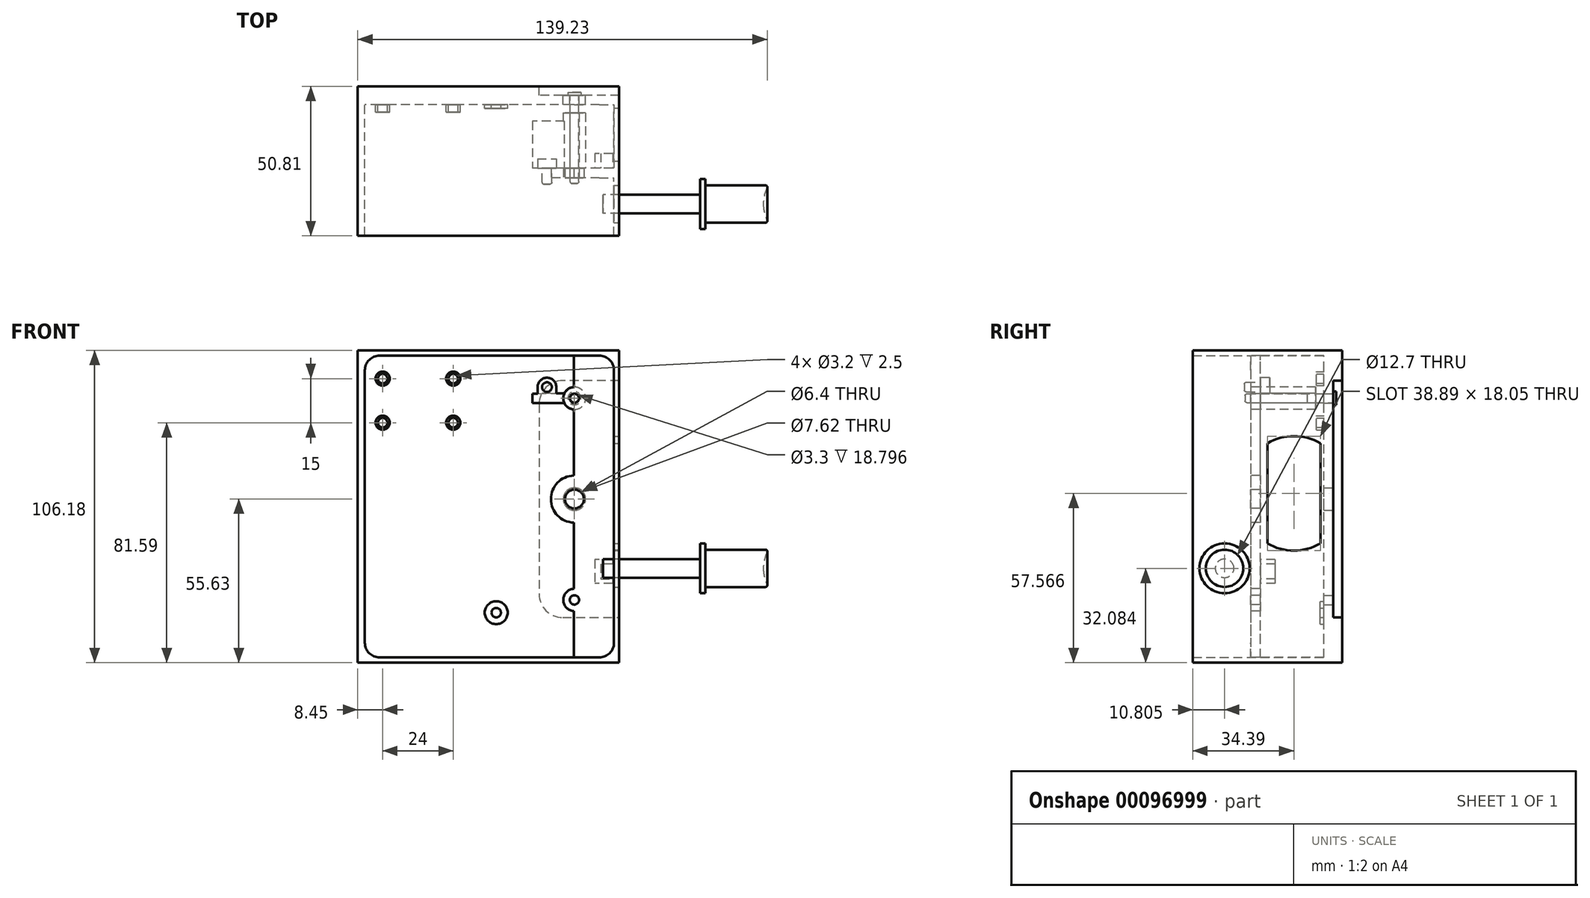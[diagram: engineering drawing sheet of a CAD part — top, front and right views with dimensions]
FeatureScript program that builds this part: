
annotation { "Feature Type Name" : "Feature", "Feature Type Description" : "" }
export const myFeature = defineFeature(function(context is Context, id is Id, definition is map)
    precondition{}
    {
        {
            var Q0;
            Q0=qCreatedBy(makeId("Front.planeOp"),FACE);
            var sketch = newSketch(context, id + "F0", { "sketchPlane" : qUnion([Q0])});
            skLineSegment(sketch, "E0", {"start": v(42.67, 51.3) * mm, "end": v(42.67, -51.3) * mm});
            skLineSegment(sketch, "E1", {"start": v(-44.45, 53.09) * mm, "end": v(-44.45, -53.09) * mm});
            skLineSegment(sketch, "E2", {"start": v(44.45, 53.09) * mm, "end": v(-44.45, 53.09) * mm});
            skLineSegment(sketch, "E3", {"start": v(44.45, -53.09) * mm, "end": v(-44.45, -53.09) * mm});
            skLineSegment(sketch, "E4", {"start": v(44.45, 53.09) * mm, "end": v(44.45, -53.09) * mm});
            skCircle(sketch, "E5", {"center": v(29.2, -31.75) * mm, "radius": 1.59 * mm});
            skCircle(sketch, "E6", {"center": v(-6.73, -45.9) * mm, "radius": 1.59 * mm});
            skLineSegment(sketch, "E7", {"start": v(36.07, 28.96) * mm, "end": v(36.07, 24.38) * mm});
            skLineSegment(sketch, "E8", {"start": v(42.21, 30.73) * mm, "end": v(36.1, 30.73) * mm});
            skLineSegment(sketch, "E9", {"start": v(42.21, 22.6) * mm, "end": v(36.1, 22.6) * mm});
            skLineSegment(sketch, "E10", {"start": v(38.13, 29.21) * mm, "end": v(38.13, 28.96) * mm});
            skLineSegment(sketch, "E11", {"start": v(36.07, 28.96) * mm, "end": v(38.15, 28.96) * mm});
            skLineSegment(sketch, "E12", {"start": v(36.07, 24.38) * mm, "end": v(38.15, 24.38) * mm});
            skLineSegment(sketch, "E13", {"start": v(42.21, 30.73) * mm, "end": v(42.21, 29.21) * mm});
            skLineSegment(sketch, "E14", {"start": v(42.21, 29.21) * mm, "end": v(38.13, 29.21) * mm});
            skLineSegment(sketch, "E15", {"start": v(42.21, 24.13) * mm, "end": v(38.13, 24.13) * mm});
            skLineSegment(sketch, "E16", {"start": v(42.21, 24.13) * mm, "end": v(42.21, 22.6) * mm});
            skLineSegment(sketch, "E17", {"start": v(36.1, 30.73) * mm, "end": v(36.1, 28.96) * mm});
            skLineSegment(sketch, "E18", {"start": v(38.15, 28.96) * mm, "end": v(38.15, 24.38) * mm});
            skLineSegment(sketch, "E19", {"start": v(38.13, 24.13) * mm, "end": v(38.13, 24.38) * mm});
            skLineSegment(sketch, "E20", {"start": v(36.1, 22.6) * mm, "end": v(36.1, 24.38) * mm});
            skLineSegment(sketch, "E21", {"start": v(36.07, -24.38) * mm, "end": v(36.07, -19.81) * mm});
            skLineSegment(sketch, "E22", {"start": v(42.21, -26.16) * mm, "end": v(36.1, -26.16) * mm});
            skLineSegment(sketch, "E23", {"start": v(42.21, -18.03) * mm, "end": v(36.1, -18.03) * mm});
            skLineSegment(sketch, "E24", {"start": v(38.13, -24.64) * mm, "end": v(38.13, -24.38) * mm});
            skLineSegment(sketch, "E25", {"start": v(36.07, -24.38) * mm, "end": v(38.15, -24.38) * mm});
            skLineSegment(sketch, "E26", {"start": v(36.07, -19.81) * mm, "end": v(38.15, -19.81) * mm});
            skLineSegment(sketch, "E27", {"start": v(42.21, -26.16) * mm, "end": v(42.21, -24.64) * mm});
            skLineSegment(sketch, "E28", {"start": v(42.21, -24.64) * mm, "end": v(38.13, -24.64) * mm});
            skLineSegment(sketch, "E29", {"start": v(42.21, -19.56) * mm, "end": v(38.13, -19.56) * mm});
            skLineSegment(sketch, "E30", {"start": v(42.21, -19.56) * mm, "end": v(42.21, -18.03) * mm});
            skLineSegment(sketch, "E31", {"start": v(36.1, -26.16) * mm, "end": v(36.1, -24.38) * mm});
            skLineSegment(sketch, "E32", {"start": v(38.15, -24.38) * mm, "end": v(38.15, -19.81) * mm});
            skLineSegment(sketch, "E33", {"start": v(38.13, -19.56) * mm, "end": v(38.13, -19.81) * mm});
            skLineSegment(sketch, "E34", {"start": v(36.1, -18.03) * mm, "end": v(36.1, -19.81) * mm});
            skLineSegment(sketch, "E35", {"start": v(42.67, 51.3) * mm, "end": v(-42.04, 51.3) * mm});
            skLineSegment(sketch, "E36", {"start": v(-42.04, 51.3) * mm, "end": v(-42.04, -51.3) * mm});
            skLineSegment(sketch, "E37", {"start": v(42.67, -51.3) * mm, "end": v(-42.04, -51.3) * mm});
            skLineSegment(sketch, "E38", {"start": v(42.67, -19.44) * mm, "end": v(44.45, -19.44) * mm});
            skLineSegment(sketch, "E39", {"start": v(42.67, -22.62) * mm, "end": v(44.45, -22.62) * mm});
            skCircle(sketch, "E40", {"center": v(29.2, 2.54) * mm, "radius": 4.76 * mm});
            skCircle(sketch, "E41", {"center": v(29.2, 2.54) * mm, "radius": 3.81 * mm});
            skLineSegment(sketch, "E42", {"start": v(29.2, 2.54) * mm, "end": v(29.2, 21.89) * mm, "construction": true});
            skCircle(sketch, "E43", {"center": v(29.2, 36.83) * mm, "radius": 1.59 * mm, "construction": true});
            skSolve(sketch);
        }
        {
            var Q0;
            Q0=qCreatedBy(makeId("Front.planeOp"),FACE);
            var sketch = newSketch(context, id + "F1", { "sketchPlane" : qUnion([Q0])});
            skLineSegment(sketch, "E44", {"start": v(-44.45, 53.09) * mm, "end": v(44.45, 53.09) * mm});
            skLineSegment(sketch, "E45", {"start": v(44.45, 53.09) * mm, "end": v(44.45, -53.09) * mm});
            skLineSegment(sketch, "E46", {"start": v(44.45, -53.09) * mm, "end": v(-44.45, -53.09) * mm});
            skLineSegment(sketch, "E47", {"start": v(-44.45, -53.09) * mm, "end": v(-44.45, 53.09) * mm});
            skSolve(sketch);
        }
        {
            var Q0;
            Q0 = qSketchRegion(id + "F1", true);
            var Q1;
            Q1=sQuery(id+"F0.wireOp",EDGE,"E2");
            var Q2;
            Q2=sQuery(id+"F0.wireOp",EDGE,"E1");
            var Q3;
            Q3=sQuery(id+"F0.wireOp",EDGE,"E4");
            var Q4;
            Q4=sQuery(id+"F0.wireOp",EDGE,"E3");
            extrude(context, id + "F2", {"entities" : qUnion([Q0]), "surfaceEntities" : qUnion([Q1, Q2, Q3, Q4]), "depth" : 19.68 * mm});
        }
        {
            var Q0;
            Q0=qCreatedBy(makeId("Front.planeOp"),FACE);
            var sketch = newSketch(context, id + "F3", { "sketchPlane" : qUnion([Q0])});
            skLineSegment(sketch, "E48.0.0", {"start": v(44.45, 53.09) * mm, "end": v(-44.45, 53.09) * mm});
            skLineSegment(sketch, "E48.0.1", {"start": v(-44.45, 53.09) * mm, "end": v(-44.45, -53.09) * mm});
            skLineSegment(sketch, "E48.0.2", {"start": v(-44.45, -53.09) * mm, "end": v(44.45, -53.09) * mm});
            skLineSegment(sketch, "E48.0.3", {"start": v(44.45, -53.09) * mm, "end": v(44.45, 53.09) * mm});
            skSolve(sketch);
        }
        {
            var Q0;
            Q0 = qSketchRegion(id + "F3", true);
            extrude(context, id + "F4", {"entities" : qUnion([Q0]), "operationType" : NewBodyOperationType.ADD, "oppositeDirection" : true, "depth" : 31.1 * mm});
        }
        {
            var Q0;
            Q0=qCreatedBy(makeId("Front.planeOp"),FACE);
            var sketch = newSketch(context, id + "F5", { "sketchPlane" : qUnion([Q0])});
            skLineSegment(sketch, "E49.0", {"start": v(-42.04, 46.3) * mm, "end": v(-42.04, -46.3) * mm});
            skLineSegment(sketch, "E50.0", {"start": v(37.67, 51.3) * mm, "end": v(-37.04, 51.3) * mm});
            skLineSegment(sketch, "E51.0", {"start": v(42.67, 46.3) * mm, "end": v(42.67, -46.3) * mm});
            skLineSegment(sketch, "E52.0", {"start": v(37.67, -51.3) * mm, "end": v(-37.04, -51.3) * mm});
            skPoint(sketch, "E53.visualSharp", {"position": v(-42.04, 51.3) * mm});
            skArc(sketch, "E53.filletArc", {"start": v(-37.04, 51.3) * mm, "mid": v(-40.58, 49.84) * mm, "end": v(-42.04, 46.3) * mm});
            skPoint(sketch, "E54.visualSharp", {"position": v(42.67, 51.3) * mm});
            skArc(sketch, "E54.filletArc", {"start": v(42.67, 46.3) * mm, "mid": v(41.2, 49.84) * mm, "end": v(37.67, 51.3) * mm});
            skPoint(sketch, "E55.visualSharp", {"position": v(-42.04, -51.3) * mm});
            skArc(sketch, "E55.filletArc", {"start": v(-42.04, -46.3) * mm, "mid": v(-40.58, -49.84) * mm, "end": v(-37.04, -51.3) * mm});
            skPoint(sketch, "E56.visualSharp", {"position": v(42.67, -51.3) * mm});
            skArc(sketch, "E56.filletArc", {"start": v(37.67, -51.3) * mm, "mid": v(41.2, -49.84) * mm, "end": v(42.67, -46.3) * mm});
            skSolve(sketch);
        }
        {
            var Q0;
            Q0 = qSketchRegion(id + "F5", true);
            extrude(context, id + "F6", {"entities" : qUnion([Q0]), "operationType" : NewBodyOperationType.REMOVE, "endBound" : BoundingType.THROUGH_ALL, "depth" : 25 * mm});
        }
        {
            var Q0;
            Q0=qCreatedBy(makeId("Front.planeOp"),FACE);
            cPlane(context, id + "F7", {"entities" : qUnion([Q0]), "cplaneType" : CPlaneType.OFFSET, "offset" : 8.88 * mm, "width" : 150 * mm, "height" : 150 * mm});
        }
        {
            var Q0;
            Q0=makeQuery(id+"F4.boolean.opBoolean","MERGE",FACE,{"derivedFrom":[makeQuery(id+"F2.opExtrude","SWEPT_FACE",FACE,{"disambiguationData":[OSD([sQuery(id+"F1.wireOp",EDGE,"E45")])]}),makeQuery(id+"F4.opExtrude","SWEPT_FACE",FACE,{"disambiguationData":[OSD([sQuery(id+"F3.wireOp",EDGE,"E48.0.3")])]})]});
            var sketch = newSketch(context, id + "F8", { "sketchPlane" : qUnion([Q0])});
            skCircle(sketch, "E57", {"center": v(-8.88, -21) * mm, "radius": 6.35 * mm});
            skSolve(sketch);
        }
        {
            var Q0;
            Q0 = qSketchRegion(id + "F8", true);
            extrude(context, id + "F9", {"entities" : qUnion([Q0]), "operationType" : NewBodyOperationType.REMOVE, "endBound" : BoundingType.UP_TO_NEXT, "oppositeDirection" : true, "depth" : 25 * mm});
        }
        {
            var Q0;
            Q0=qCreatedBy(makeId("Front.planeOp"),FACE);
            cPlane(context, id + "F10", {"entities" : qUnion([Q0]), "cplaneType" : CPlaneType.OFFSET, "offset" : 3.27 * mm, "oppositeDirection" : true, "width" : 150 * mm, "height" : 150 * mm});
        }
        {
            var Q0;
            Q0=qCreatedBy(id+"F10.planeOp",FACE);
            var sketch = newSketch(context, id + "F11", { "sketchPlane" : qUnion([Q0])});
            skArc(sketch, "E58.0.0", {"start": v(-37.04, 51.3) * mm, "mid": v(-40.58, 49.84) * mm, "end": v(-42.04, 46.3) * mm});
            skLineSegment(sketch, "E58.0.1", {"start": v(-42.04, 46.3) * mm, "end": v(-42.04, -46.3) * mm});
            skArc(sketch, "E58.0.2", {"start": v(-42.04, -46.3) * mm, "mid": v(-40.58, -49.84) * mm, "end": v(-37.04, -51.3) * mm});
            skLineSegment(sketch, "E58.0.3", {"start": v(-37.04, -51.3) * mm, "end": v(37.67, -51.3) * mm});
            skArc(sketch, "E58.0.4", {"start": v(37.67, -51.3) * mm, "mid": v(41.2, -49.84) * mm, "end": v(42.67, -46.3) * mm});
            skLineSegment(sketch, "E58.0.5", {"start": v(42.67, -46.3) * mm, "end": v(42.67, 46.3) * mm});
            skArc(sketch, "E58.0.6", {"start": v(42.67, 46.3) * mm, "mid": v(41.2, 49.84) * mm, "end": v(37.67, 51.3) * mm});
            skLineSegment(sketch, "E58.0.7", {"start": v(37.67, 51.3) * mm, "end": v(-37.04, 51.3) * mm});
            skSolve(sketch);
        }
        {
            var Q0;
            Q0 = qSketchRegion(id + "F11", true);
            extrude(context, id + "F12", {"entities" : qUnion([Q0]), "operationType" : NewBodyOperationType.REMOVE, "oppositeDirection" : true, "depth" : 21.59 * mm});
        }
        {
            var Q0;
            Q0=makeQuery(id+"F0.imprint","IMPRINT",FACE,{"disambiguationData":[TD([[makeQuery(id+"F0.imprint","IMPRINT",EDGE,{"derivedFrom":sQuery(id+"F0.wireOp",EDGE,"E5")}),1.0]])]});
            var sketch = newSketch(context, id + "F13", { "sketchPlane" : qUnion([Q0])});
            skLineSegment(sketch, "E59.0", {"start": v(29, 51.3) * mm, "end": v(-37.04, 51.3) * mm});
            skLineSegment(sketch, "E60.0", {"start": v(-42.04, 46.3) * mm, "end": v(-42.04, -46.3) * mm});
            skLineSegment(sketch, "E61.0", {"start": v(29, -51.3) * mm, "end": v(-37.04, -51.3) * mm});
            skArc(sketch, "E62.0", {"start": v(-42.04, 46.3) * mm, "mid": v(-40.58, 49.84) * mm, "end": v(-37.04, 51.3) * mm});
            skPoint(sketch, "E63.orphan", {"position": v(-42.04, 51.3) * mm});
            skPoint(sketch, "E64.orphan", {"position": v(-42.04, -51.3) * mm});
            skArc(sketch, "E65.0", {"start": v(-37.04, -51.3) * mm, "mid": v(-40.58, -49.84) * mm, "end": v(-42.04, -46.3) * mm});
            skCircle(sketch, "E66.0", {"center": v(29.2, 2.54) * mm, "radius": 3.81 * mm, "construction": true});
            skCircle(sketch, "E67.0", {"center": v(29.2, -31.75) * mm, "radius": 1.59 * mm, "construction": true});
            skLineSegment(sketch, "E68", {"start": v(29, 51.3) * mm, "end": v(29, 40.62) * mm});
            skArc(sketch, "E69", {"start": v(29, 40.62) * mm, "mid": v(25.4, 36.83) * mm, "end": v(29, 33.04) * mm});
            skArc(sketch, "E70", {"start": v(29, 10.54) * mm, "mid": v(21.2, 2.54) * mm, "end": v(29, -5.46) * mm});
            skArc(sketch, "E71", {"start": v(29, -27.96) * mm, "mid": v(25.4, -31.75) * mm, "end": v(29, -35.54) * mm});
            skPoint(sketch, "E72.orphan", {"position": v(42.67, 51.3) * mm});
            skPoint(sketch, "E73.orphan", {"position": v(42.67, -51.3) * mm});
            skLineSegment(sketch, "E74.trimOffspring", {"start": v(29, 33.04) * mm, "end": v(29, 10.54) * mm});
            skLineSegment(sketch, "E75.trimOffspring", {"start": v(29, -5.46) * mm, "end": v(29, -27.96) * mm});
            skLineSegment(sketch, "E76.trimOffspring", {"start": v(29, -35.54) * mm, "end": v(29, -51.3) * mm});
            skCircle(sketch, "E77.0", {"center": v(29.2, -31.75) * mm, "radius": 1.59 * mm});
            skCircle(sketch, "E78.0", {"center": v(29.2, 36.83) * mm, "radius": 1.59 * mm});
            skCircle(sketch, "E79", {"center": v(29.2, 2.54) * mm, "radius": 3.2 * mm});
            skSolve(sketch);
        }
        {
            var Q0;
            Q0 = qSketchRegion(id + "F13", true);
            extrude(context, id + "F14", {"entities" : qUnion([Q0]), "operationType" : NewBodyOperationType.REMOVE, "endBound" : BoundingType.UP_TO_NEXT, "oppositeDirection" : true, "depth" : 25 * mm});
        }
        {
            var Q0;
            Q0=qCreatedBy(makeId("Front.planeOp"),FACE);
            cPlane(context, id + "F15", {"entities" : qUnion([Q0]), "cplaneType" : CPlaneType.OFFSET, "offset" : 14.7 * mm, "oppositeDirection" : true, "width" : 150 * mm, "height" : 150 * mm});
        }
        {
            var Q0;
            Q0=makeQuery(id+"F4.boolean.opBoolean","MERGE",FACE,{"derivedFrom":[makeQuery(id+"F2.opExtrude","SWEPT_FACE",FACE,{"disambiguationData":[OSD([sQuery(id+"F1.wireOp",EDGE,"E45")])]}),makeQuery(id+"F4.opExtrude","SWEPT_FACE",FACE,{"disambiguationData":[OSD([sQuery(id+"F3.wireOp",EDGE,"E48.0.3")])]})]});
            var sketch = newSketch(context, id + "F16", { "sketchPlane" : qUnion([Q0])});
            skLineSegment(sketch, "E80", {"start": v(14.7, 41.38) * mm, "end": v(14.7, -48.23) * mm, "construction": true});
            skLineSegment(sketch, "E81", {"start": v(-22.52, 4.48) * mm, "end": v(53.42, 4.48) * mm, "construction": true});
            skLineSegment(sketch, "E82.left", {"start": v(23.72, -12.54) * mm, "end": v(23.72, 21.5) * mm});
            skLineSegment(sketch, "E82.right", {"start": v(5.67, -12.54) * mm, "end": v(5.67, 21.5) * mm});
            skPoint(sketch, "E82.middle", {"position": v(14.7, 4.48) * mm});
            skArc(sketch, "E83", {"start": v(23.73, 21.5) * mm, "mid": v(14.7, 23.92) * mm, "end": v(5.67, 21.5) * mm});
            skArc(sketch, "E84.trimOffspring", {"start": v(5.67, -12.54) * mm, "mid": v(14.7, -14.97) * mm, "end": v(23.72, -12.54) * mm});
            skPoint(sketch, "E85", {"position": v(14.7, 23.92) * mm});
            skPoint(sketch, "E86", {"position": v(14.7, -14.97) * mm});
            skSolve(sketch);
        }
        {
            var Q0;
            Q0 = qSketchRegion(id + "F16", true);
            extrude(context, id + "F17", {"entities" : qUnion([Q0]), "operationType" : NewBodyOperationType.REMOVE, "oppositeDirection" : true, "depth" : 2 * mm});
        }
        {
            var Q0;
            Q0=makeQuery(id+"F4.opExtrude","CAP_FACE",FACE,{"disambiguationData":[OSD([sQuery(id+"F3.wireOp",EDGE,"E48.0.0"),sQuery(id+"F3.wireOp",EDGE,"E48.0.1"),sQuery(id+"F3.wireOp",EDGE,"E48.0.2"),sQuery(id+"F3.wireOp",EDGE,"E48.0.3")])],"isStart":false});
            var sketch = newSketch(context, id + "F18", { "sketchPlane" : qUnion([Q0])});
            skLineSegment(sketch, "E87.0", {"start": v(-44.45, 42.83) * mm, "end": v(-44.45, -37.75) * mm});
            skLineSegment(sketch, "E88", {"start": v(-44.45, 42.83) * mm, "end": v(-25.21, 42.83) * mm});
            skLineSegment(sketch, "E89", {"start": v(-17.2, 34.83) * mm, "end": v(-17.2, -29.75) * mm});
            skLineSegment(sketch, "E90", {"start": v(-25.2, -37.75) * mm, "end": v(-44.45, -37.75) * mm});
            skPoint(sketch, "E91.orphan", {"position": v(-44.45, 53.09) * mm});
            skPoint(sketch, "E92.orphan", {"position": v(-44.45, -53.09) * mm});
            skPoint(sketch, "E93.visualSharp", {"position": v(-17.21, 42.83) * mm});
            skArc(sketch, "E93.filletArc", {"start": v(-17.2, 34.83) * mm, "mid": v(-19.55, 40.49) * mm, "end": v(-25.21, 42.83) * mm});
            skPoint(sketch, "E94.visualSharp", {"position": v(-17.2, -37.75) * mm});
            skArc(sketch, "E94.filletArc", {"start": v(-25.2, -37.75) * mm, "mid": v(-19.55, -35.4) * mm, "end": v(-17.2, -29.75) * mm});
            skLineSegment(sketch, "E95", {"start": v(-17.2, 2.54) * mm, "end": v(-86.8, 2.54) * mm, "construction": true});
            skPoint(sketch, "E95.endSnap0", {"position": v(-17.2, 2.54) * mm});
            skSolve(sketch);
        }
        {
            var Q0;
            Q0 = qSketchRegion(id + "F18", true);
            extrude(context, id + "F19", {"entities" : qUnion([Q0]), "operationType" : NewBodyOperationType.REMOVE, "oppositeDirection" : true, "depth" : 3 * mm});
        }
        {
            var Q0;
            Q0=makeQuery(id+"F19.boolean.opBoolean","COPY",FACE,{"derivedFrom":makeQuery(id+"F19.opExtrude","CAP_FACE",FACE,{"disambiguationData":[OSD([sQuery(id+"F18.wireOp",EDGE,"E87.0"),sQuery(id+"F18.wireOp",EDGE,"E88"),sQuery(id+"F18.wireOp",EDGE,"E89"),sQuery(id+"F18.wireOp",EDGE,"E90"),sQuery(id+"F18.wireOp",EDGE,"E93.filletArc"),sQuery(id+"F18.wireOp",EDGE,"E94.filletArc")])],"isStart":false})});
            var sketch = newSketch(context, id + "F20", { "sketchPlane" : qUnion([Q0])});
            skCircle(sketch, "E96.0", {"center": v(-29.2, 2.54) * mm, "radius": 3.81 * mm});
            skCircle(sketch, "E97.0", {"center": v(-29.2, 36.83) * mm, "radius": 1.59 * mm});
            skCircle(sketch, "E98.0", {"center": v(-29.2, -31.75) * mm, "radius": 1.59 * mm});
            skSolve(sketch);
        }
        {
            var Q0;
            Q0 = qSketchRegion(id + "F20", true);
            extrude(context, id + "F21", {"entities" : qUnion([Q0]), "operationType" : NewBodyOperationType.REMOVE, "oppositeDirection" : true, "depth" : 4 * mm});
        }
        {
            var Q0;
            Q0=qCreatedBy(id+"F7.planeOp",FACE);
            var sketch = newSketch(context, id + "F22", { "sketchPlane" : qUnion([Q0])});
            skLineSegment(sketch, "E99.0", {"start": v(44.45, -14.66) * mm, "end": v(44.45, -27.36) * mm, "construction": true});
            skPoint(sketch, "E100", {"position": v(44.45, -21) * mm});
            skLineSegment(sketch, "E101", {"start": v(-16.64, -21) * mm, "end": v(94.45, -21) * mm, "construction": true});
            skLineSegment(sketch, "E102", {"start": v(38.9, -21) * mm, "end": v(38.9, -17.83) * mm});
            skLineSegment(sketch, "E103", {"start": v(38.9, -17.83) * mm, "end": v(71.9, -17.83) * mm});
            skLineSegment(sketch, "E104", {"start": v(71.9, -17.83) * mm, "end": v(71.9, -12.5) * mm});
            skLineSegment(sketch, "E105", {"start": v(71.9, -12.5) * mm, "end": v(73.68, -12.5) * mm});
            skLineSegment(sketch, "E106", {"start": v(73.68, -12.5) * mm, "end": v(73.68, -14.66) * mm});
            skLineSegment(sketch, "E107", {"start": v(73.68, -14.66) * mm, "end": v(95.18, -14.66) * mm});
            skLineSegment(sketch, "E108", {"start": v(38.9, -21) * mm, "end": v(93.45, -21) * mm});
            skArc(sketch, "E109", {"start": v(95.18, -14.66) * mm, "mid": v(93.9, -17.71) * mm, "end": v(93.45, -21) * mm});
            skPoint(sketch, "E110.end.orphan", {"position": v(94.45, -21) * mm});
            skSolve(sketch);
        }
        {
            var Q0;
            Q0 = qSketchRegion(id + "F22", true);
            var Q1;
            Q1=sQuery(id+"F22.wireOp",EDGE,"E101");
            revolve(context, id + "F23", {"entities" : qUnion([Q0]), "axis" : qUnion([Q1]), "revolveType" : RevolveType.FULL});
        }
        {
            var Q0;
            Q0=makeQuery(id+"F23.opRevolve","SWEPT_FACE",FACE,{"disambiguationData":[OSD([sQuery(id+"F22.wireOp",EDGE,"E109")])]});
            fillet(context, id + "F24", {"entities" : qUnion([Q0]), "radius" : 0.6 * mm, "tangentPropagation" : true, "allowEdgeOverflow" : false});
        }
        {
            var Q0;
            Q0=makeQuery(id+"F12.boolean.opBoolean","COPY",FACE,{"derivedFrom":makeQuery(id+"F12.opExtrude","CAP_FACE",FACE,{"disambiguationData":[OSD([sQuery(id+"F11.wireOp",EDGE,"E58.0.0"),sQuery(id+"F11.wireOp",EDGE,"E58.0.1"),sQuery(id+"F11.wireOp",EDGE,"E58.0.2"),sQuery(id+"F11.wireOp",EDGE,"E58.0.3"),sQuery(id+"F11.wireOp",EDGE,"E58.0.4"),sQuery(id+"F11.wireOp",EDGE,"E58.0.5"),sQuery(id+"F11.wireOp",EDGE,"E58.0.6"),sQuery(id+"F11.wireOp",EDGE,"E58.0.7")])],"isStart":true})});
            var sketch = newSketch(context, id + "F25", { "sketchPlane" : qUnion([Q0])});
            skCircle(sketch, "E111", {"center": v(-29.2, 36.83) * mm, "radius": 1.65 * mm});
            skArc(sketch, "E112", {"start": v(-25.77, 38.46) * mm, "mid": v(-33.02, 36.8) * mm, "end": v(-25.75, 35.24) * mm});
            skLineSegment(sketch, "E113", {"start": v(-33.02, 36.83) * mm, "end": v(-12.46, 36.83) * mm, "construction": true});
            skLineSegment(sketch, "E114", {"start": v(-25.77, 38.46) * mm, "end": v(-23.04, 38.45) * mm});
            skLineSegment(sketch, "E115", {"start": v(-25.75, 35.24) * mm, "end": v(-14.99, 35.24) * mm});
            skLineSegment(sketch, "E116", {"start": v(-14.99, 35.24) * mm, "end": v(-14.99, 38.42) * mm});
            skCircle(sketch, "E117", {"center": v(-19.86, 40.61) * mm, "radius": 1.65 * mm});
            skArc(sketch, "E118", {"start": v(-16.69, 40.61) * mm, "mid": v(-19.85, 43.79) * mm, "end": v(-23.04, 40.64) * mm});
            skLineSegment(sketch, "E119", {"start": v(-16.69, 40.61) * mm, "end": v(-16.69, 38.42) * mm});
            skLineSegment(sketch, "E120", {"start": v(-23.04, 40.64) * mm, "end": v(-23.04, 38.45) * mm});
            skLineSegment(sketch, "E121.trimOffspring", {"start": v(-16.69, 38.42) * mm, "end": v(-14.99, 38.42) * mm});
            skSolve(sketch);
        }
        {
            var Q0;
            {var subQ7=sQuery(id+"F25.wireOp",EDGE,"E112");Q0=makeQuery(id+"F25.imprint","IMPRINT",FACE,{"disambiguationData":[TD([[makeQuery(id+"F25.imprint","IMPRINT",EDGE,{"derivedFrom":subQ7}),-1.0]])]});}
            var sketch = newSketch(context, id + "F26", { "sketchPlane" : qUnion([Q0])});
            skCircle(sketch, "E122.0", {"center": v(-29.2, 36.83) * mm, "radius": 1.65 * mm});
            skCircle(sketch, "E123.converted", {"center": v(-29.2, 36.83) * mm, "radius": 3.81 * mm});
            skPoint(sketch, "E124.orphan", {"position": v(-25.77, 38.46) * mm});
            skSolve(sketch);
        }
        {
            var Q0;
            Q0 = qSketchRegion(id + "F26", true);
            extrude(context, id + "F27", {"entities" : qUnion([Q0]), "depth" : 18.8 * mm});
        }
        {
            var Q0;
            {var subQ7=sQuery(id+"F25.wireOp",EDGE,"E112");Q0=makeQuery(id+"F25.imprint","IMPRINT",FACE,{"disambiguationData":[TD([[makeQuery(id+"F25.imprint","IMPRINT",EDGE,{"derivedFrom":subQ7}),-1.0]])]});}
            var sketch = newSketch(context, id + "F28", { "sketchPlane" : qUnion([Q0])});
            skLineSegment(sketch, "E125.0", {"start": v(-25.75, 35.24) * mm, "end": v(-14.99, 35.24) * mm});
            skLineSegment(sketch, "E126.0", {"start": v(-14.99, 35.24) * mm, "end": v(-14.99, 38.42) * mm});
            skLineSegment(sketch, "E127", {"start": v(-25.77, 38.46) * mm, "end": v(-25.75, 35.24) * mm});
            skLineSegment(sketch, "E128.0", {"start": v(-25.77, 38.46) * mm, "end": v(-14.99, 38.42) * mm});
            skPoint(sketch, "E129.orphan", {"position": v(-23.04, 38.45) * mm});
            skSolve(sketch);
        }
        {
            var Q0;
            Q0 = qSketchRegion(id + "F28", true);
            extrude(context, id + "F29", {"entities" : qUnion([Q0]), "operationType" : NewBodyOperationType.ADD, "depth" : 16 * mm});
        }
        {
            var Q0;
            {var subQ7=sQuery(id+"F25.wireOp",EDGE,"E112");Q0=makeQuery(id+"F25.imprint","IMPRINT",FACE,{"disambiguationData":[TD([[makeQuery(id+"F25.imprint","IMPRINT",EDGE,{"derivedFrom":subQ7}),-1.0]])]});}
            var sketch = newSketch(context, id + "F30", { "sketchPlane" : qUnion([Q0])});
            skLineSegment(sketch, "E130.0", {"start": v(-16.69, 40.61) * mm, "end": v(-16.69, 38.42) * mm});
            skLineSegment(sketch, "E131.0", {"start": v(-23.04, 40.64) * mm, "end": v(-23.04, 38.45) * mm});
            skArc(sketch, "E132.0", {"start": v(-16.69, 40.61) * mm, "mid": v(-19.85, 43.79) * mm, "end": v(-23.04, 40.64) * mm});
            skLineSegment(sketch, "E133", {"start": v(-16.69, 38.42) * mm, "end": v(-23.04, 38.45) * mm});
            skSolve(sketch);
        }
        {
            var Q0;
            Q0 = qSketchRegion(id + "F30", true);
            extrude(context, id + "F31", {"entities" : qUnion([Q0]), "operationType" : NewBodyOperationType.ADD, "depth" : 3.2 * mm});
        }
        {
            var Q0;
            {var subQ7=sQuery(id+"F25.wireOp",EDGE,"E112");Q0=makeQuery(id+"F25.imprint","IMPRINT",FACE,{"disambiguationData":[TD([[makeQuery(id+"F25.imprint","IMPRINT",EDGE,{"derivedFrom":subQ7}),-1.0]])]});}
            var sketch = newSketch(context, id + "F32", { "sketchPlane" : qUnion([Q0])});
            skCircle(sketch, "E134.0", {"center": v(-19.86, 40.61) * mm, "radius": 1.65 * mm});
            skSolve(sketch);
        }
        {
            var Q0;
            Q0 = qSketchRegion(id + "F32", true);
            extrude(context, id + "F33", {"entities" : qUnion([Q0]), "operationType" : NewBodyOperationType.ADD, "oppositeDirection" : true, "depth" : 5.4 * mm});
        }
        {
            var Q0;
            Q0=makeQuery(id+"F33.opExtrude","CAP_EDGE",EDGE,{"disambiguationData":[OSD([sQuery(id+"F32.wireOp",EDGE,"E134.0")])],"isStart":false});
            fillet(context, id + "F34", {"entities" : qUnion([Q0]), "radius" : 0.6 * mm, "tangentPropagation" : true, "allowEdgeOverflow" : false});
        }
        {
            var Q0;
            Q0=makeQuery(id+"F12.boolean.opBoolean","COPY",FACE,{"derivedFrom":makeQuery(id+"F12.opExtrude","CAP_FACE",FACE,{"disambiguationData":[OSD([sQuery(id+"F11.wireOp",EDGE,"E58.0.0"),sQuery(id+"F11.wireOp",EDGE,"E58.0.1"),sQuery(id+"F11.wireOp",EDGE,"E58.0.2"),sQuery(id+"F11.wireOp",EDGE,"E58.0.3"),sQuery(id+"F11.wireOp",EDGE,"E58.0.4"),sQuery(id+"F11.wireOp",EDGE,"E58.0.5"),sQuery(id+"F11.wireOp",EDGE,"E58.0.6"),sQuery(id+"F11.wireOp",EDGE,"E58.0.7")])],"isStart":false})});
            var sketch = newSketch(context, id + "F35", { "sketchPlane" : qUnion([Q0])});
            skCircle(sketch, "E135", {"center": v(2.62, -36.1) * mm, "radius": 1.6 * mm});
            skCircle(sketch, "E136", {"center": v(2.62, -36.1) * mm, "radius": 3.9 * mm});
            skCircle(sketch, "E137.0", {"center": v(29.2, 2.54) * mm, "radius": 3.2 * mm, "construction": true});
            skSolve(sketch);
        }
        {
            var Q0;
            Q0 = qSketchRegion(id + "F35", true);
            extrude(context, id + "F36", {"entities" : qUnion([Q0]), "operationType" : NewBodyOperationType.ADD, "depth" : 1.2 * mm});
        }
        {
            var Q0;
            {var subQ3=sQuery(id+"F11.wireOp",EDGE,"E58.0.4");Q0=makeQuery(id+"F25.imprint","IMPRINT",FACE,{"disambiguationData":[TD([[makeQuery(id+"F25.imprint","IMPRINT",EDGE,{"derivedFrom":makeQuery(id+"F12.boolean.opBoolean","COPY",EDGE,{"derivedFrom":makeQuery(id+"F12.opExtrude","CAP_EDGE",EDGE,{"disambiguationData":[OSD([subQ3])],"isStart":true})})}),-1.0]])]});}
            var sketch = newSketch(context, id + "F37", { "sketchPlane" : qUnion([Q0])});
            skLineSegment(sketch, "E138.0", {"start": v(-42.21, -26.16) * mm, "end": v(-36.1, -26.16) * mm});
            skLineSegment(sketch, "E139.0", {"start": v(-42.21, -18.03) * mm, "end": v(-36.1, -18.03) * mm});
            skLineSegment(sketch, "E140", {"start": v(-36.1, -18.03) * mm, "end": v(-36.1, -26.16) * mm});
            skLineSegment(sketch, "E141", {"start": v(-42.21, -18.03) * mm, "end": v(-42.21, -19.56) * mm});
            skLineSegment(sketch, "E142", {"start": v(-42.21, -19.56) * mm, "end": v(-38.13, -19.56) * mm});
            skLineSegment(sketch, "E143", {"start": v(-38.13, -19.56) * mm, "end": v(-38.13, -24.64) * mm});
            skLineSegment(sketch, "E144", {"start": v(-38.13, -24.64) * mm, "end": v(-42.21, -24.64) * mm});
            skLineSegment(sketch, "E145", {"start": v(-42.21, -24.64) * mm, "end": v(-42.21, -26.16) * mm});
            skSolve(sketch);
        }
        {
            var Q0;
            Q0 = qSketchRegion(id + "F37", true);
            extrude(context, id + "F38", {"entities" : qUnion([Q0]), "depth" : 5 * mm});
        }
        {
            var Q0;
            Q0=makeQuery(id+"F19.boolean.opBoolean","COPY",FACE,{"derivedFrom":makeQuery(id+"F19.opExtrude","CAP_FACE",FACE,{"disambiguationData":[OSD([sQuery(id+"F18.wireOp",EDGE,"E87.0"),sQuery(id+"F18.wireOp",EDGE,"E88"),sQuery(id+"F18.wireOp",EDGE,"E89"),sQuery(id+"F18.wireOp",EDGE,"E90"),sQuery(id+"F18.wireOp",EDGE,"E93.filletArc"),sQuery(id+"F18.wireOp",EDGE,"E94.filletArc")])],"isStart":false})});
            var sketch = newSketch(context, id + "F39", { "sketchPlane" : qUnion([Q0])});
            skCircle(sketch, "E146", {"center": v(-29.2, 36.83) * mm, "radius": 1.5 * mm});
            skSolve(sketch);
        }
        {
            var Q0;
            Q0 = qSketchRegion(id + "F39", true);
            extrude(context, id + "F40", {"entities" : qUnion([Q0]), "oppositeDirection" : true, "depth" : 30 * mm});
        }
        {
            var Q0;
            Q0=makeQuery(id+"F40.opExtrude","CAP_EDGE",EDGE,{"disambiguationData":[OSD([sQuery(id+"F39.wireOp",EDGE,"E146")])],"isStart":false});
            fillet(context, id + "F41", {"entities" : qUnion([Q0]), "radius" : 0.6 * mm, "tangentPropagation" : true, "allowEdgeOverflow" : false});
        }
        {
            var Q0;
            Q0=makeQuery(id+"F19.boolean.opBoolean","COPY",FACE,{"derivedFrom":makeQuery(id+"F19.opExtrude","CAP_FACE",FACE,{"disambiguationData":[OSD([sQuery(id+"F18.wireOp",EDGE,"E87.0"),sQuery(id+"F18.wireOp",EDGE,"E88"),sQuery(id+"F18.wireOp",EDGE,"E89"),sQuery(id+"F18.wireOp",EDGE,"E90"),sQuery(id+"F18.wireOp",EDGE,"E93.filletArc"),sQuery(id+"F18.wireOp",EDGE,"E94.filletArc")])],"isStart":false})});
            var sketch = newSketch(context, id + "F42", { "sketchPlane" : qUnion([Q0])});
            skCircle(sketch, "E147", {"center": v(-29.2, 36.83) * mm, "radius": 2.25 * mm});
            skSolve(sketch);
        }
        {
            var Q0;
            Q0 = qSketchRegion(id + "F42", true);
            extrude(context, id + "F43", {"entities" : qUnion([Q0]), "operationType" : NewBodyOperationType.ADD, "depth" : 1 * mm});
        }
        {
            var Q0;
            {var subQ0=sQuery(id+"F11.wireOp",EDGE,"E58.0.3");var subQ1=sQuery(id+"F11.wireOp",EDGE,"E58.0.2");var subQ2=sQuery(id+"F11.wireOp",EDGE,"E58.0.0");var subQ3=sQuery(id+"F11.wireOp",EDGE,"E58.0.4");var subQ4=sQuery(id+"F11.wireOp",EDGE,"E58.0.1");var subQ5=sQuery(id+"F11.wireOp",EDGE,"E58.0.5");var subQ6=sQuery(id+"F11.wireOp",EDGE,"E58.0.6");var subQ7=sQuery(id+"F11.wireOp",EDGE,"E58.0.7");Q0=makeQuery(id+"F36.boolean.opBoolean","SPLIT",FACE,{"disambiguationData":[TD([makeQuery(id+"F6.boolean.opBoolean","COPY",FACE,{"derivedFrom":makeQuery(id+"F6.opExtrude","SWEPT_FACE",FACE,{"disambiguationData":[OSD([sQuery(id+"F5.wireOp",EDGE,"E49.0")])]})})])],"derivedFrom":makeQuery(id+"F12.boolean.opBoolean","COPY",FACE,{"derivedFrom":makeQuery(id+"F12.opExtrude","CAP_FACE",FACE,{"disambiguationData":[OSD([subQ2,subQ4,subQ1,subQ0,subQ3,subQ5,subQ6,subQ7])],"isStart":false})})});}
            var sketch = newSketch(context, id + "F44", { "sketchPlane" : qUnion([Q0])});
            skLineSegment(sketch, "E148", {"start": v(-24, 51.3) * mm, "end": v(-24, -24.6) * mm, "construction": true});
            skLineSegment(sketch, "E149", {"start": v(-39.67, 36) * mm, "end": v(-3.08, 36) * mm, "construction": true});
            skCircle(sketch, "E150", {"center": v(-36, 43.5) * mm, "radius": 2.4 * mm});
            skCircle(sketch, "E151", {"center": v(-36, 28.5) * mm, "radius": 2.4 * mm});
            skCircle(sketch, "E152", {"center": v(-12, 43.5) * mm, "radius": 2.4 * mm});
            skCircle(sketch, "E153", {"center": v(-12, 28.5) * mm, "radius": 2.4 * mm});
            skCircle(sketch, "E154", {"center": v(-36, 43.5) * mm, "radius": 1.6 * mm});
            skCircle(sketch, "E155", {"center": v(-12, 43.5) * mm, "radius": 1.6 * mm});
            skCircle(sketch, "E156", {"center": v(-36, 28.5) * mm, "radius": 1.6 * mm});
            skCircle(sketch, "E157", {"center": v(-12, 28.5) * mm, "radius": 1.6 * mm});
            skSolve(sketch);
        }
        {
            var Q0;
            Q0 = qSketchRegion(id + "F44", true);
            extrude(context, id + "F45", {"entities" : qUnion([Q0]), "operationType" : NewBodyOperationType.ADD, "depth" : 2.5 * mm});
        }
    });
